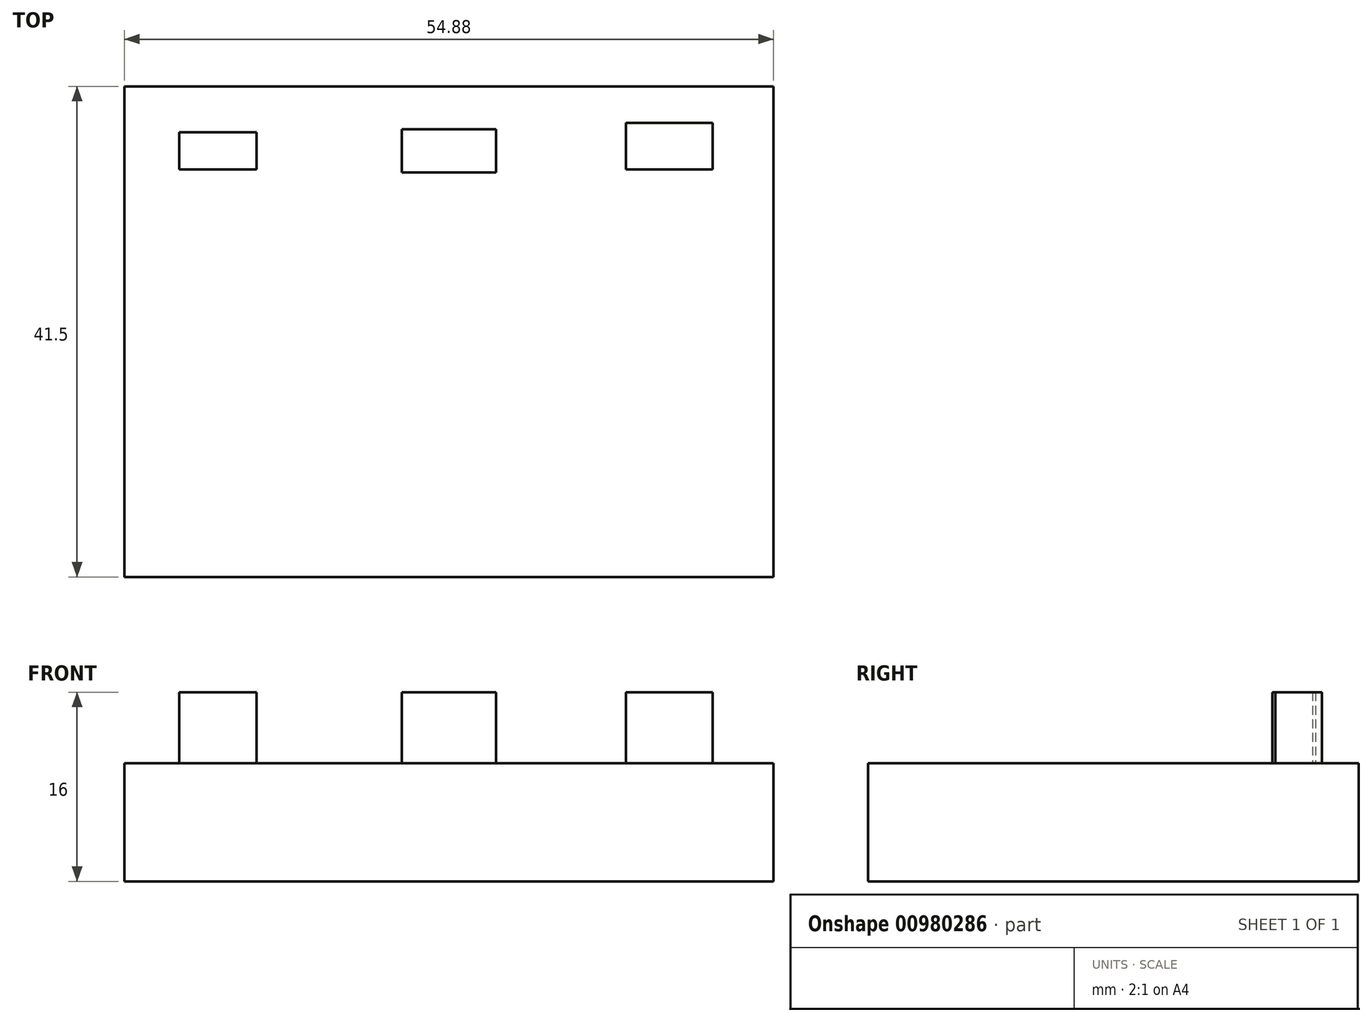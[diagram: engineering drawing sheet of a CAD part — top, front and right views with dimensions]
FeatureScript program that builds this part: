
annotation { "Feature Type Name" : "Feature", "Feature Type Description" : "" }
export const myFeature = defineFeature(function(context is Context, id is Id, definition is map)
    precondition{}
    {
        {
            var Q0;
            Q0=qCreatedBy(makeId("Top.planeOp"),FACE);
            var sketch = newSketch(context, id + "F0", { "sketchPlane" : qUnion([Q0])});
            skLineSegment(sketch, "E0.bottom", {"start": v(27.44, 20.75) * mm, "end": v(-27.44, 20.75) * mm});
            skLineSegment(sketch, "E0.top", {"start": v(27.44, -20.75) * mm, "end": v(-27.44, -20.75) * mm});
            skLineSegment(sketch, "E0.left", {"start": v(27.44, 20.75) * mm, "end": v(27.44, -20.75) * mm});
            skLineSegment(sketch, "E0.right", {"start": v(-27.44, 20.75) * mm, "end": v(-27.44, -20.75) * mm});
            skPoint(sketch, "E0.middle", {"position": v(0, 0) * mm});
            skSolve(sketch);
        }
        {
            var Q0;
            Q0 = qSketchRegion(id + "F0", true);
            extrude(context, id + "F1", {"entities" : qUnion([Q0]), "depth" : 10 * mm, "offsetDistance" : 25 * mm});
        }
        {
            var Q0;
            Q0=makeQuery(id+"F1.opExtrude","CAP_FACE",FACE,{"disambiguationData":[OSD([sQuery(id+"F0.wireOp",EDGE,"E0.bottom"),sQuery(id+"F0.wireOp",EDGE,"E0.top"),sQuery(id+"F0.wireOp",EDGE,"E0.left"),sQuery(id+"F0.wireOp",EDGE,"E0.right")])],"isStart":false});
            var sketch = newSketch(context, id + "F2", { "sketchPlane" : qUnion([Q0])});
            skLineSegment(sketch, "E1.bottom", {"start": v(-16.27, 16.86) * mm, "end": v(-22.8, 16.86) * mm});
            skLineSegment(sketch, "E1.top", {"start": v(-16.27, 13.72) * mm, "end": v(-22.8, 13.72) * mm});
            skLineSegment(sketch, "E1.left", {"start": v(-16.27, 16.86) * mm, "end": v(-16.27, 13.72) * mm});
            skLineSegment(sketch, "E1.right", {"start": v(-22.8, 16.86) * mm, "end": v(-22.8, 13.72) * mm});
            skPoint(sketch, "E1.middle", {"position": v(-19.54, 15.29) * mm});
            skLineSegment(sketch, "E2.bottom", {"start": v(4, 17.12) * mm, "end": v(-4, 17.12) * mm});
            skLineSegment(sketch, "E2.top", {"start": v(4, 13.46) * mm, "end": v(-4, 13.46) * mm});
            skLineSegment(sketch, "E2.left", {"start": v(4, 17.12) * mm, "end": v(4, 13.46) * mm});
            skLineSegment(sketch, "E2.right", {"start": v(-4, 17.12) * mm, "end": v(-4, 13.46) * mm});
            skPoint(sketch, "E2.middle", {"position": v(0, 15.29) * mm});
            skLineSegment(sketch, "E3.bottom", {"start": v(22.3, 17.64) * mm, "end": v(14.98, 17.64) * mm});
            skLineSegment(sketch, "E3.top", {"start": v(22.3, 13.72) * mm, "end": v(14.98, 13.72) * mm});
            skLineSegment(sketch, "E3.left", {"start": v(22.3, 17.64) * mm, "end": v(22.3, 13.72) * mm});
            skLineSegment(sketch, "E3.right", {"start": v(14.98, 17.64) * mm, "end": v(14.98, 13.72) * mm});
            skPoint(sketch, "E3.middle", {"position": v(18.64, 15.68) * mm});
            skSolve(sketch);
        }
        {
            var Q0;
            Q0 = qSketchRegion(id + "F2", true);
            extrude(context, id + "F3", {"entities" : qUnion([Q0]), "operationType" : NewBodyOperationType.ADD, "depth" : 6 * mm, "offsetDistance" : 25 * mm});
        }
    });
